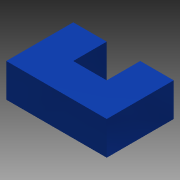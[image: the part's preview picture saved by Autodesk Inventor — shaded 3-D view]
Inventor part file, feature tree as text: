
AUTODESK INVENTOR PART (.ipt)
format: ipt  version: 2015 (Build 190159000, 159)  size: 83,968 bytes
history: native  units: in
note: dims shown in document units (in); Inventor stores cm internally (conversion verified against a paired STEP export)
features: extrude x1, sketch x1
ambient origin geometry x8: Origin, YZ Plane, XZ Plane, XY Plane, X Axis, Y Axis, Z Axis, Center Point
bodies: Solid1 (feature_tree)
feature tree (2):
  extrude  "Extrusion1"  Depth=1.5in
  sketch  "Sketch1"  dims[d0=2.25in d1=1.5in d2=0.75in d3=0.75in d4=0.75in d5=0.75in d6=0.75in d7=0.75in d8=0.0in]
